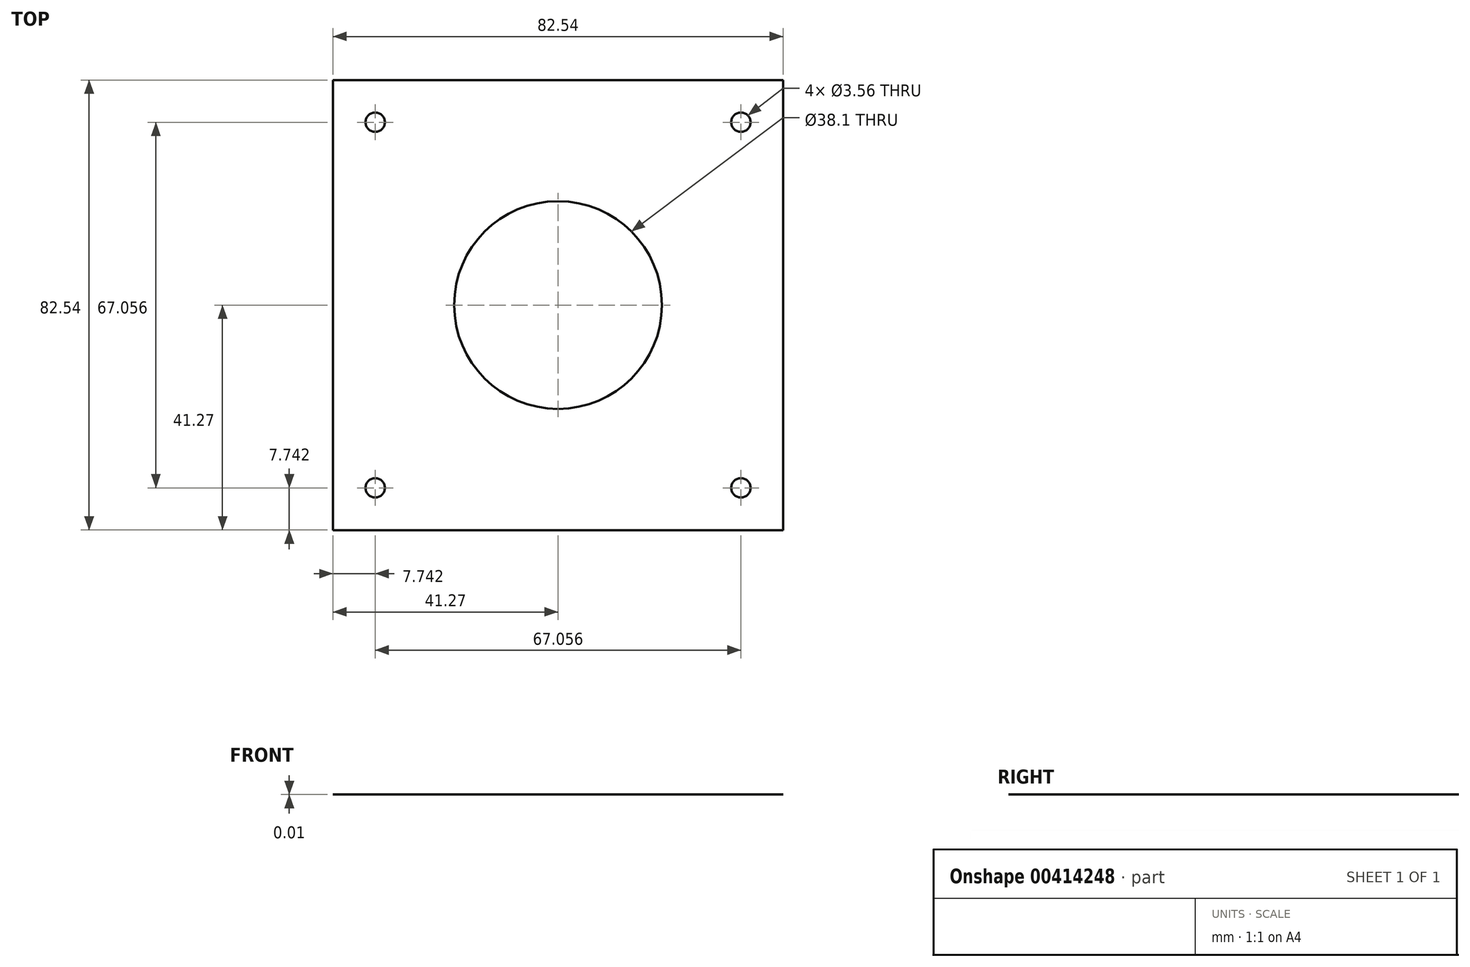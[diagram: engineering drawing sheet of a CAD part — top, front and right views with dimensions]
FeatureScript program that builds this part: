
annotation { "Feature Type Name" : "Feature", "Feature Type Description" : "" }
export const myFeature = defineFeature(function(context is Context, id is Id, definition is map)
    precondition{}
    {
        {
            var Q0;
            Q0=qCreatedBy(makeId("Top.planeOp"),FACE);
            var sketch = newSketch(context, id + "F0", { "sketchPlane" : qUnion([Q0])});
            skLineSegment(sketch, "E0.bottom", {"start": v(41.28, 41.27) * mm, "end": v(-41.28, 41.28) * mm});
            skLineSegment(sketch, "E0.top", {"start": v(41.28, -41.28) * mm, "end": v(-41.28, -41.28) * mm});
            skLineSegment(sketch, "E0.left", {"start": v(41.28, 41.28) * mm, "end": v(41.28, -41.28) * mm});
            skLineSegment(sketch, "E0.right", {"start": v(-41.28, 41.28) * mm, "end": v(-41.28, -41.28) * mm});
            skCircle(sketch, "E1", {"center": v(0, 0) * mm, "radius": 19.05 * mm});
            skLineSegment(sketch, "E2", {"start": v(0, 0) * mm, "end": v(0, 25) * mm, "construction": true});
            skLineSegment(sketch, "E3", {"start": v(0, 25) * mm, "end": v(25, 25) * mm, "construction": true});
            skLineSegment(sketch, "E4", {"start": v(0, 0) * mm, "end": v(41.28, 41.28) * mm, "construction": true});
            skCircle(sketch, "E5", {"center": v(33.53, 33.53) * mm, "radius": 1.78 * mm});
            skCircle(sketch, "E6.1.0", {"center": v(-33.53, 33.53) * mm, "radius": 1.78 * mm});
            skCircle(sketch, "E6.2.0", {"center": v(-33.53, -33.53) * mm, "radius": 1.78 * mm});
            skCircle(sketch, "E6.3.0", {"center": v(33.53, -33.53) * mm, "radius": 1.78 * mm});
            skLineSegment(sketch, "E7", {"start": v(0, 0) * mm, "end": v(41.28, 0) * mm, "construction": true});
            skSolve(sketch);
        }
        {
            var Q0;
            Q0=makeQuery(id+"F0.imprint","IMPRINT",FACE,{"disambiguationData":[TD([[makeQuery(id+"F0.imprint","IMPRINT",EDGE,{"derivedFrom":sQuery(id+"F0.wireOp",EDGE,"E0.bottom")}),1.0]])]});
            extrude(context, id + "F1", {"entities" : qUnion([Q0]), "depth" : 1 / 101.6 * mm});
        }
    });
